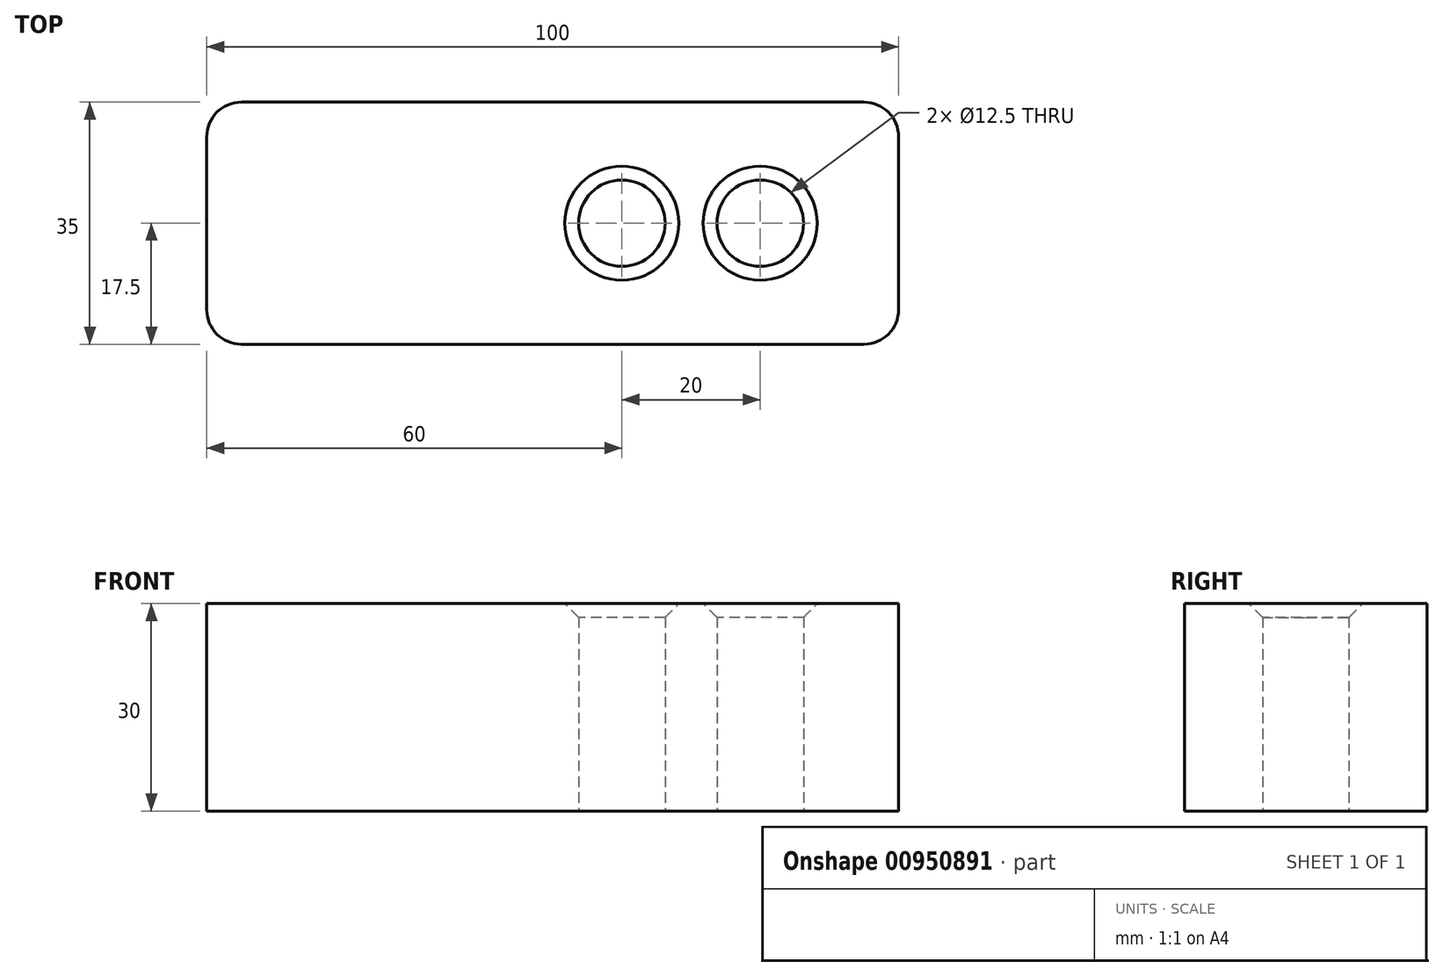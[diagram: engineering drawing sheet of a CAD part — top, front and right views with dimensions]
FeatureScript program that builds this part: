
annotation { "Feature Type Name" : "Feature", "Feature Type Description" : "" }
export const myFeature = defineFeature(function(context is Context, id is Id, definition is map)
    precondition{}
    {
        {
            var Q0;
            Q0=qCreatedBy(makeId("Top.planeOp"),FACE);
            var sketch = newSketch(context, id + "F0", { "sketchPlane" : qUnion([Q0])});
            skLineSegment(sketch, "E0.bottom", {"start": v(45, 17.5) * mm, "end": v(-45, 17.5) * mm});
            skLineSegment(sketch, "E0.top", {"start": v(45, -17.5) * mm, "end": v(-45, -17.5) * mm});
            skLineSegment(sketch, "E0.left", {"start": v(50, 12.5) * mm, "end": v(50, -12.5) * mm});
            skLineSegment(sketch, "E0.right", {"start": v(-50, 12.5) * mm, "end": v(-50, -12.5) * mm});
            skPoint(sketch, "E0.middle", {"position": v(0, 0) * mm});
            skCircle(sketch, "E1", {"center": v(-30, 0) * mm, "radius": 6.25 * mm});
            skCircle(sketch, "E2", {"center": v(-10, 0) * mm, "radius": 6.25 * mm});
            skCircle(sketch, "E3.MirrorC", {"center": v(30, 0) * mm, "radius": 6.25 * mm});
            skCircle(sketch, "E4.MirrorC", {"center": v(10, 0) * mm, "radius": 6.25 * mm});
            skPoint(sketch, "E5.visualSharp", {"position": v(-50, 17.5) * mm});
            skArc(sketch, "E5.filletArc", {"start": v(-45, 17.5) * mm, "mid": v(-48.54, 16.04) * mm, "end": v(-50, 12.5) * mm});
            skPoint(sketch, "E6.visualSharp", {"position": v(-50, -17.5) * mm});
            skArc(sketch, "E6.filletArc", {"start": v(-50, -12.5) * mm, "mid": v(-48.54, -16.04) * mm, "end": v(-45, -17.5) * mm});
            skPoint(sketch, "E7.visualSharp", {"position": v(50, 17.5) * mm});
            skArc(sketch, "E7.filletArc", {"start": v(50, 12.5) * mm, "mid": v(48.54, 16.04) * mm, "end": v(45, 17.5) * mm});
            skPoint(sketch, "E8.visualSharp", {"position": v(50, -17.5) * mm});
            skArc(sketch, "E8.filletArc", {"start": v(45, -17.5) * mm, "mid": v(48.54, -16.04) * mm, "end": v(50, -12.5) * mm});
            skSolve(sketch);
        }
        {
            var Q0;
            Q0=makeQuery(id+"F0.imprint","IMPRINT",FACE,{"disambiguationData":[TD([[makeQuery(id+"F0.imprint","IMPRINT",EDGE,{"derivedFrom":sQuery(id+"F0.wireOp",EDGE,"E1")}),1.0]])]});
            var Q1;
            Q1=makeQuery(id+"F0.imprint","IMPRINT",FACE,{"disambiguationData":[TD([[makeQuery(id+"F0.imprint","IMPRINT",EDGE,{"derivedFrom":sQuery(id+"F0.wireOp",EDGE,"E2")}),1.0]])]});
            var Q2;
            Q2=makeQuery(id+"F0.imprint","IMPRINT",FACE,{"disambiguationData":[TD([[makeQuery(id+"F0.imprint","IMPRINT",EDGE,{"derivedFrom":sQuery(id+"F0.wireOp",EDGE,"E4.MirrorC")}),-1.0]])]});
            var Q3;
            Q3=makeQuery(id+"F0.imprint","IMPRINT",FACE,{"disambiguationData":[TD([[makeQuery(id+"F0.imprint","IMPRINT",EDGE,{"derivedFrom":sQuery(id+"F0.wireOp",EDGE,"E3.MirrorC")}),-1.0]])]});
            extrude(context, id + "F1", {"entities" : qUnion([Q0, Q1, Q2, Q3]), "depth" : 30 * mm, "offsetDistance" : 25 * mm});
        }
        {
            var Q0;
            Q0=makeQuery(id+"F0.imprint","IMPRINT",FACE,{"disambiguationData":[TD([[makeQuery(id+"F0.imprint","IMPRINT",EDGE,{"derivedFrom":sQuery(id+"F0.wireOp",EDGE,"E0.bottom")}),1.0]])]});
            extrude(context, id + "F2", {"entities" : qUnion([Q0]), "operationType" : NewBodyOperationType.ADD, "depth" : 4 * mm, "offsetDistance" : 25 * mm});
        }
        {
            var Q0;
            Q0=makeQuery(id+"F1.opExtrude","CAP_EDGE",EDGE,{"disambiguationData":[OSD([sQuery(id+"F0.wireOp",EDGE,"E1")])],"isStart":false});
            var Q1;
            Q1=makeQuery(id+"F1.opExtrude","CAP_EDGE",EDGE,{"disambiguationData":[OSD([sQuery(id+"F0.wireOp",EDGE,"E2")])],"isStart":false});
            var Q2;
            Q2=makeQuery(id+"F1.opExtrude","CAP_EDGE",EDGE,{"disambiguationData":[OSD([sQuery(id+"F0.wireOp",EDGE,"E4.MirrorC")])],"isStart":false});
            var Q3;
            Q3=makeQuery(id+"F1.opExtrude","CAP_EDGE",EDGE,{"disambiguationData":[OSD([sQuery(id+"F0.wireOp",EDGE,"E3.MirrorC")])],"isStart":false});
            chamfer(context, id + "F3", {"entities" : qUnion([Q0, Q1, Q2, Q3]), "width" : 2 * mm, "tangentPropagation" : true});
        }
    });
